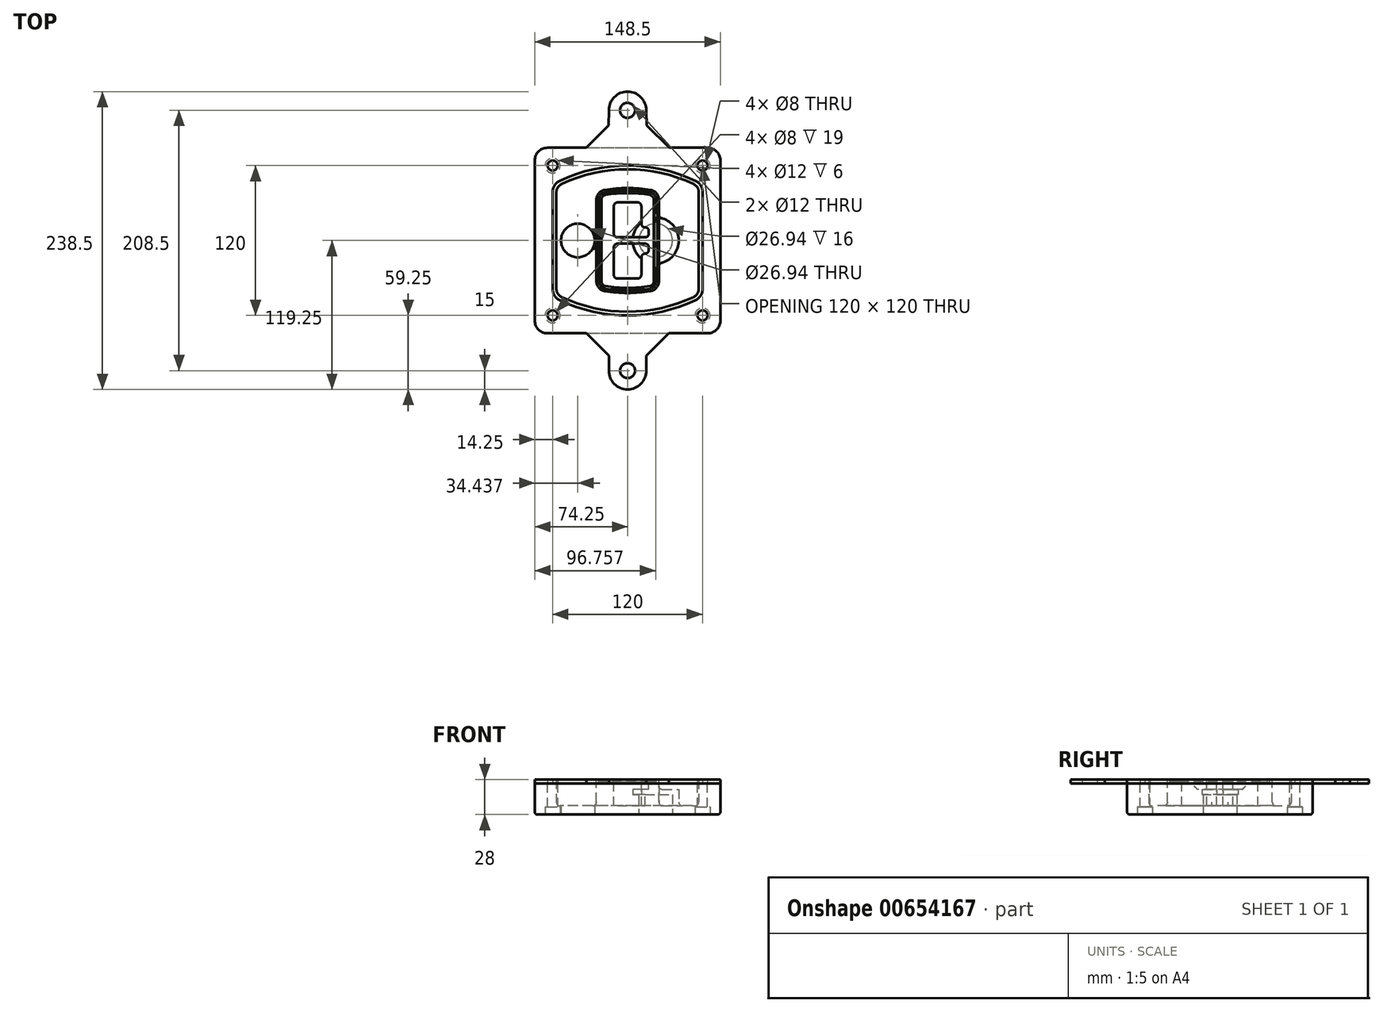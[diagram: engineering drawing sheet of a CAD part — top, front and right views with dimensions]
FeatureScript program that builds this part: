
annotation { "Feature Type Name" : "Feature", "Feature Type Description" : "" }
export const myFeature = defineFeature(function(context is Context, id is Id, definition is map)
    precondition{}
    {
        {
            var Q0;
            Q0=qCreatedBy(makeId("Top.planeOp"),FACE);
            var sketch = newSketch(context, id + "F0", { "sketchPlane" : qUnion([Q0])});
            skPoint(sketch, "E0.rect.middle", {"position": v(0, 0) * mm});
            skLineSegment(sketch, "E1.bottom", {"start": v(-64.25, -74.25) * mm, "end": v(64.25, -74.25) * mm});
            skLineSegment(sketch, "E1.top", {"start": v(-64.25, 74.25) * mm, "end": v(64.25, 74.25) * mm});
            skLineSegment(sketch, "E1.left", {"start": v(-74.25, -64.25) * mm, "end": v(-74.25, 64.25) * mm});
            skLineSegment(sketch, "E1.right", {"start": v(74.25, -64.25) * mm, "end": v(74.25, 64.25) * mm});
            skLineSegment(sketch, "E2", {"start": v(-74.25, 74.25) * mm, "end": v(74.25, -74.25) * mm, "construction": true});
            skLineSegment(sketch, "E3", {"start": v(74.25, 74.25) * mm, "end": v(-74.25, -74.25) * mm, "construction": true});
            skCircle(sketch, "E4", {"center": v(-60, 60) * mm, "radius": 4 * mm});
            skCircle(sketch, "E5", {"center": v(60, 60) * mm, "radius": 4 * mm});
            skCircle(sketch, "E6", {"center": v(60, -60) * mm, "radius": 4 * mm});
            skCircle(sketch, "E7", {"center": v(-60, -60) * mm, "radius": 4 * mm});
            skLineSegment(sketch, "E8", {"start": v(-60, 60) * mm, "end": v(60, 60) * mm, "construction": true});
            skLineSegment(sketch, "E9", {"start": v(60, 60) * mm, "end": v(60, -60) * mm, "construction": true});
            skLineSegment(sketch, "E10", {"start": v(60, -60) * mm, "end": v(-60, -60) * mm, "construction": true});
            skLineSegment(sketch, "E11", {"start": v(-60, -60) * mm, "end": v(-60, 60) * mm, "construction": true});
            skLineSegment(sketch, "E12", {"start": v(-60, 38.83) * mm, "end": v(-60, -38.83) * mm});
            skLineSegment(sketch, "E13", {"start": v(60, 38.83) * mm, "end": v(60, -38.83) * mm});
            skArc(sketch, "E14", {"start": v(54.26, 47.88) * mm, "mid": v(0, 60) * mm, "end": v(-54.26, 47.88) * mm});
            skArc(sketch, "E15", {"start": v(-54.26, -47.88) * mm, "mid": v(0, -60) * mm, "end": v(54.26, -47.88) * mm});
            skLineSegment(sketch, "E16", {"start": v(-60, 0) * mm, "end": v(60, 0) * mm, "construction": true});
            skPoint(sketch, "E17.visualSharp", {"position": v(-60, -45) * mm});
            skArc(sketch, "E17.filletArc", {"start": v(-60, -38.83) * mm, "mid": v(-58.44, -44.2) * mm, "end": v(-54.26, -47.88) * mm});
            skPoint(sketch, "E18.visualSharp", {"position": v(-60, 45) * mm});
            skArc(sketch, "E18.filletArc", {"start": v(-54.26, 47.88) * mm, "mid": v(-58.44, 44.2) * mm, "end": v(-60, 38.83) * mm});
            skPoint(sketch, "E19.visualSharp", {"position": v(60, 45) * mm});
            skArc(sketch, "E19.filletArc", {"start": v(60, 38.83) * mm, "mid": v(58.44, 44.2) * mm, "end": v(54.26, 47.88) * mm});
            skPoint(sketch, "E20.visualSharp", {"position": v(60, -45) * mm});
            skArc(sketch, "E20.filletArc", {"start": v(54.26, -47.88) * mm, "mid": v(58.44, -44.2) * mm, "end": v(60, -38.83) * mm});
            skPoint(sketch, "E21.visualSharp", {"position": v(-74.25, 74.25) * mm});
            skArc(sketch, "E21.filletArc", {"start": v(-64.25, 74.25) * mm, "mid": v(-71.32, 71.32) * mm, "end": v(-74.25, 64.25) * mm});
            skPoint(sketch, "E22.visualSharp", {"position": v(74.25, 74.25) * mm});
            skArc(sketch, "E22.filletArc", {"start": v(74.25, 64.25) * mm, "mid": v(71.32, 71.32) * mm, "end": v(64.25, 74.25) * mm});
            skPoint(sketch, "E23.visualSharp", {"position": v(74.25, -74.25) * mm});
            skArc(sketch, "E23.filletArc", {"start": v(64.25, -74.25) * mm, "mid": v(71.32, -71.32) * mm, "end": v(74.25, -64.25) * mm});
            skPoint(sketch, "E24.visualSharp", {"position": v(-74.25, -74.25) * mm});
            skArc(sketch, "E24.filletArc", {"start": v(-74.25, -64.25) * mm, "mid": v(-71.32, -71.32) * mm, "end": v(-64.25, -74.25) * mm});
            skArc(sketch, "E25.0", {"start": v(57, 38.83) * mm, "mid": v(55.9, 42.58) * mm, "end": v(52.98, 45.17) * mm});
            skLineSegment(sketch, "E25.1", {"start": v(57, 38.83) * mm, "end": v(57, -38.83) * mm});
            skArc(sketch, "E25.2", {"start": v(52.98, -45.17) * mm, "mid": v(55.9, -42.58) * mm, "end": v(57, -38.83) * mm});
            skArc(sketch, "E25.3", {"start": v(-52.98, -45.17) * mm, "mid": v(0, -57) * mm, "end": v(52.98, -45.17) * mm});
            skArc(sketch, "E25.4", {"start": v(-57, -38.83) * mm, "mid": v(-55.9, -42.58) * mm, "end": v(-52.98, -45.17) * mm});
            skArc(sketch, "E25.5", {"start": v(52.98, 45.17) * mm, "mid": v(0, 57) * mm, "end": v(-52.98, 45.17) * mm});
            skLineSegment(sketch, "E25.6", {"start": v(-57, 38.83) * mm, "end": v(-57, -38.83) * mm});
            skArc(sketch, "E25.7", {"start": v(-52.98, 45.17) * mm, "mid": v(-55.9, 42.58) * mm, "end": v(-57, 38.83) * mm});
            skArc(sketch, "E26.0", {"start": v(-55.96, 51.5) * mm, "mid": v(-61.82, 46.33) * mm, "end": v(-64, 38.83) * mm});
            skArc(sketch, "E26.1", {"start": v(55.96, 51.5) * mm, "mid": v(0, 64) * mm, "end": v(-55.96, 51.5) * mm});
            skArc(sketch, "E26.2", {"start": v(64, 38.83) * mm, "mid": v(61.82, 46.33) * mm, "end": v(55.96, 51.5) * mm});
            skLineSegment(sketch, "E26.3", {"start": v(64, 38.83) * mm, "end": v(64, -38.83) * mm});
            skArc(sketch, "E26.4", {"start": v(55.96, -51.5) * mm, "mid": v(61.82, -46.33) * mm, "end": v(64, -38.83) * mm});
            skLineSegment(sketch, "E26.5", {"start": v(-64, 38.83) * mm, "end": v(-64, -38.83) * mm});
            skArc(sketch, "E26.6", {"start": v(-55.96, -51.5) * mm, "mid": v(0, -64) * mm, "end": v(55.96, -51.5) * mm});
            skArc(sketch, "E26.7", {"start": v(-64, -38.83) * mm, "mid": v(-61.82, -46.33) * mm, "end": v(-55.96, -51.5) * mm});
            skLineSegment(sketch, "E27", {"start": v(-33.13, 74.25) * mm, "end": v(-15.13, 92.25) * mm});
            skArc(sketch, "E28", {"start": v(15, 104.25) * mm, "mid": v(0, 119.25) * mm, "end": v(-15, 104.25) * mm});
            skCircle(sketch, "E29", {"center": v(0, 104.25) * mm, "radius": 6 * mm});
            skLineSegment(sketch, "E30", {"start": v(0, 104.25) * mm, "end": v(0, 74.25) * mm, "construction": true});
            skLineSegment(sketch, "E31", {"start": v(15.3, 92.25) * mm, "end": v(33.3, 74.25) * mm});
            skLineSegment(sketch, "E32", {"start": v(0, -74.25) * mm, "end": v(0, -104.25) * mm, "construction": true});
            skCircle(sketch, "E33", {"center": v(0, -104.25) * mm, "radius": 6 * mm});
            skArc(sketch, "E34", {"start": v(15, -104.25) * mm, "mid": v(0, -119.25) * mm, "end": v(-15, -104.25) * mm});
            skLineSegment(sketch, "E35", {"start": v(15, -104.25) * mm, "end": v(15, -92.25) * mm});
            skLineSegment(sketch, "E36", {"start": v(-15, -104.25) * mm, "end": v(-15, -92.25) * mm});
            skLineSegment(sketch, "E37", {"start": v(-15, -92.25) * mm, "end": v(-33, -74.25) * mm});
            skLineSegment(sketch, "E38", {"start": v(15, -92.25) * mm, "end": v(33, -74.25) * mm});
            skLineSegment(sketch, "E39", {"start": v(15.3, 92.25) * mm, "end": v(15, 104.25) * mm});
            skLineSegment(sketch, "E40", {"start": v(-15.13, 92.25) * mm, "end": v(-15, 104.25) * mm});
            skSolve(sketch);
        }
        {
            var Q0;
            Q0=makeQuery(id+"F0.imprint","IMPRINT",FACE,{"disambiguationData":[TD([[makeQuery(id+"F0.imprint","IMPRINT",EDGE,{"derivedFrom":sQuery(id+"F0.wireOp",EDGE,"E1.bottom")}),1.0]])]});
            var Q1;
            Q1=makeQuery(id+"F0.imprint","IMPRINT",FACE,{"disambiguationData":[TD([[makeQuery(id+"F0.imprint","IMPRINT",EDGE,{"derivedFrom":sQuery(id+"F0.wireOp",EDGE,"E12")}),1.0]])]});
            var Q2;
            Q2=makeQuery(id+"F0.imprint","IMPRINT",FACE,{"disambiguationData":[TD([[makeQuery(id+"F0.imprint","IMPRINT",EDGE,{"derivedFrom":sQuery(id+"F0.wireOp",EDGE,"E25.0")}),1.0]])]});
            var Q3;
            Q3=makeQuery(id+"F0.imprint","IMPRINT",FACE,{"disambiguationData":[TD([[makeQuery(id+"F0.imprint","IMPRINT",EDGE,{"derivedFrom":sQuery(id+"F0.wireOp",EDGE,"E12")}),-1.0]])]});
            extrude(context, id + "F1", {"entities" : qUnion([Q0, Q1, Q2, Q3]), "oppositeDirection" : true, "depth" : 25 * mm});
        }
        {
            var Q0;
            Q0=makeQuery(id+"F0.imprint","IMPRINT",FACE,{"disambiguationData":[TD([[makeQuery(id+"F0.imprint","IMPRINT",EDGE,{"derivedFrom":sQuery(id+"F0.wireOp",EDGE,"E12")}),1.0]])]});
            extrude(context, id + "F2", {"entities" : qUnion([Q0]), "operationType" : NewBodyOperationType.ADD, "depth" : 3 * mm});
        }
        {
            var Q0;
            Q0=makeQuery(id+"F0.imprint","IMPRINT",FACE,{"disambiguationData":[TD([[makeQuery(id+"F0.imprint","IMPRINT",EDGE,{"derivedFrom":sQuery(id+"F0.wireOp",EDGE,"E25.0")}),1.0]])]});
            extrude(context, id + "F3", {"entities" : qUnion([Q0]), "operationType" : NewBodyOperationType.REMOVE, "oppositeDirection" : true, "depth" : 18 * mm});
        }
        {
            var Q0;
            Q0=makeQuery(id+"F2.opExtrude","CAP_FACE",FACE,{"disambiguationData":[OSD([sQuery(id+"F0.wireOp",EDGE,"E12"),sQuery(id+"F0.wireOp",EDGE,"E13"),sQuery(id+"F0.wireOp",EDGE,"E14"),sQuery(id+"F0.wireOp",EDGE,"E15"),sQuery(id+"F0.wireOp",EDGE,"E17.filletArc"),sQuery(id+"F0.wireOp",EDGE,"E18.filletArc"),sQuery(id+"F0.wireOp",EDGE,"E19.filletArc"),sQuery(id+"F0.wireOp",EDGE,"E20.filletArc"),sQuery(id+"F0.wireOp",EDGE,"E25.0"),sQuery(id+"F0.wireOp",EDGE,"E25.1"),sQuery(id+"F0.wireOp",EDGE,"E25.2"),sQuery(id+"F0.wireOp",EDGE,"E25.3"),sQuery(id+"F0.wireOp",EDGE,"E25.4"),sQuery(id+"F0.wireOp",EDGE,"E25.5"),sQuery(id+"F0.wireOp",EDGE,"E25.6"),sQuery(id+"F0.wireOp",EDGE,"E25.7")])],"isStart":false});
            var sketch = newSketch(context, id + "F4", { "sketchPlane" : qUnion([Q0])});
            skArc(sketch, "E41.0", {"start": v(-18.34, -40.45) * mm, "mid": v(0, -42) * mm, "end": v(18.34, -40.45) * mm});
            skArc(sketch, "E42.0", {"start": v(18.34, 40.45) * mm, "mid": v(0, 42) * mm, "end": v(-18.34, 40.45) * mm});
            skLineSegment(sketch, "E43", {"start": v(-25, 32.57) * mm, "end": v(-25, -32.57) * mm});
            skLineSegment(sketch, "E44", {"start": v(25, 32.57) * mm, "end": v(25, -32.57) * mm});
            skLineSegment(sketch, "E45", {"start": v(-25, 39.1) * mm, "end": v(25, 39.1) * mm, "construction": true});
            skLineSegment(sketch, "E46", {"start": v(-25, -39.1) * mm, "end": v(25, -39.1) * mm, "construction": true});
            skPoint(sketch, "E47.visualSharp", {"position": v(-25, 39.1) * mm});
            skArc(sketch, "E47.filletArc", {"start": v(-18.34, 40.45) * mm, "mid": v(-23.11, 37.73) * mm, "end": v(-25, 32.57) * mm});
            skPoint(sketch, "E48.visualSharp", {"position": v(25, 39.1) * mm});
            skArc(sketch, "E48.filletArc", {"start": v(25, 32.57) * mm, "mid": v(23.11, 37.73) * mm, "end": v(18.34, 40.45) * mm});
            skPoint(sketch, "E49.visualSharp", {"position": v(25, -39.1) * mm});
            skArc(sketch, "E49.filletArc", {"start": v(18.34, -40.45) * mm, "mid": v(23.11, -37.73) * mm, "end": v(25, -32.57) * mm});
            skPoint(sketch, "E50.visualSharp", {"position": v(-25, -39.1) * mm});
            skArc(sketch, "E50.filletArc", {"start": v(-25, -32.57) * mm, "mid": v(-23.11, -37.73) * mm, "end": v(-18.34, -40.45) * mm});
            skArc(sketch, "E51.0", {"start": v(52.98, 45.17) * mm, "mid": v(0, 57) * mm, "end": v(-52.98, 45.17) * mm});
            skArc(sketch, "E51.1", {"start": v(-52.98, 45.17) * mm, "mid": v(-55.9, 42.58) * mm, "end": v(-57, 38.83) * mm});
            skLineSegment(sketch, "E51.2", {"start": v(-57, 38.83) * mm, "end": v(-57, -38.83) * mm});
            skArc(sketch, "E51.3", {"start": v(-57, -38.83) * mm, "mid": v(-55.9, -42.58) * mm, "end": v(-52.98, -45.17) * mm});
            skArc(sketch, "E51.4", {"start": v(-52.98, -45.17) * mm, "mid": v(0, -57) * mm, "end": v(52.98, -45.17) * mm});
            skArc(sketch, "E51.5", {"start": v(52.98, -45.17) * mm, "mid": v(55.9, -42.58) * mm, "end": v(57, -38.83) * mm});
            skLineSegment(sketch, "E51.6", {"start": v(57, 38.83) * mm, "end": v(57, -38.83) * mm});
            skArc(sketch, "E51.7", {"start": v(57, 38.83) * mm, "mid": v(55.9, 42.58) * mm, "end": v(52.98, 45.17) * mm});
            skLineSegment(sketch, "E52.0", {"start": v(23, 32.57) * mm, "end": v(23, -32.57) * mm});
            skArc(sketch, "E52.1", {"start": v(18, -38.48) * mm, "mid": v(21.58, -36.44) * mm, "end": v(23, -32.57) * mm});
            skArc(sketch, "E52.2", {"start": v(-18, -38.48) * mm, "mid": v(0, -40) * mm, "end": v(18, -38.48) * mm});
            skArc(sketch, "E52.3", {"start": v(-23, -32.57) * mm, "mid": v(-21.58, -36.44) * mm, "end": v(-18, -38.48) * mm});
            skLineSegment(sketch, "E52.4", {"start": v(-23, 32.57) * mm, "end": v(-23, -32.57) * mm});
            skArc(sketch, "E52.5", {"start": v(23, 32.57) * mm, "mid": v(21.58, 36.44) * mm, "end": v(18, 38.48) * mm});
            skArc(sketch, "E52.6", {"start": v(-18, 38.48) * mm, "mid": v(-21.58, 36.44) * mm, "end": v(-23, 32.57) * mm});
            skArc(sketch, "E52.7", {"start": v(18, 38.48) * mm, "mid": v(0, 40) * mm, "end": v(-18, 38.48) * mm});
            skArc(sketch, "E53.0", {"start": v(21, 32.57) * mm, "mid": v(20.06, 35.15) * mm, "end": v(17.67, 36.5) * mm});
            skLineSegment(sketch, "E53.1", {"start": v(21, 32.57) * mm, "end": v(21, -32.57) * mm});
            skArc(sketch, "E53.2", {"start": v(17.67, -36.5) * mm, "mid": v(20.06, -35.15) * mm, "end": v(21, -32.57) * mm});
            skArc(sketch, "E53.3", {"start": v(-17.67, -36.5) * mm, "mid": v(0, -38) * mm, "end": v(17.67, -36.5) * mm});
            skArc(sketch, "E53.4", {"start": v(-21, -32.57) * mm, "mid": v(-20.06, -35.15) * mm, "end": v(-17.67, -36.5) * mm});
            skArc(sketch, "E53.5", {"start": v(17.67, 36.5) * mm, "mid": v(0, 38) * mm, "end": v(-17.67, 36.5) * mm});
            skLineSegment(sketch, "E53.6", {"start": v(-21, 32.57) * mm, "end": v(-21, -32.57) * mm});
            skArc(sketch, "E53.7", {"start": v(-17.67, 36.5) * mm, "mid": v(-20.06, 35.15) * mm, "end": v(-21, 32.57) * mm});
            skLineSegment(sketch, "E54", {"start": v(-25, 0) * mm, "end": v(25, 0) * mm, "construction": true});
            skLineSegment(sketch, "E55", {"start": v(-11, 5.5) * mm, "end": v(-11, 27.5) * mm});
            skLineSegment(sketch, "E56", {"start": v(-8, 30.5) * mm, "end": v(8, 30.5) * mm});
            skLineSegment(sketch, "E57", {"start": v(11, 27.5) * mm, "end": v(11, 13.5) * mm});
            skLineSegment(sketch, "E58", {"start": v(14, 10.5) * mm, "end": v(14, 10.5) * mm});
            skLineSegment(sketch, "E59", {"start": v(17, 7.5) * mm, "end": v(17, 5.5) * mm});
            skLineSegment(sketch, "E60", {"start": v(14, 2.5) * mm, "end": v(-8, 2.5) * mm});
            skPoint(sketch, "E61.visualSharp", {"position": v(-11, 30.5) * mm});
            skArc(sketch, "E61.filletArc", {"start": v(-8, 30.5) * mm, "mid": v(-10.12, 29.62) * mm, "end": v(-11, 27.5) * mm});
            skPoint(sketch, "E62.visualSharp", {"position": v(11, 30.5) * mm});
            skArc(sketch, "E62.filletArc", {"start": v(11, 27.5) * mm, "mid": v(10.12, 29.62) * mm, "end": v(8, 30.5) * mm});
            skPoint(sketch, "E63.visualSharp", {"position": v(11, 10.5) * mm});
            skArc(sketch, "E63.filletArc", {"start": v(11, 13.5) * mm, "mid": v(11.88, 11.38) * mm, "end": v(14, 10.5) * mm});
            skPoint(sketch, "E64.visualSharp", {"position": v(17, 10.5) * mm});
            skArc(sketch, "E64.filletArc", {"start": v(17, 7.5) * mm, "mid": v(16.12, 9.62) * mm, "end": v(14, 10.5) * mm});
            skPoint(sketch, "E65.visualSharp", {"position": v(17, 2.5) * mm});
            skArc(sketch, "E65.filletArc", {"start": v(14, 2.5) * mm, "mid": v(16.12, 3.38) * mm, "end": v(17, 5.5) * mm});
            skPoint(sketch, "E66.visualSharp", {"position": v(-11, 2.5) * mm});
            skArc(sketch, "E66.filletArc", {"start": v(-11, 5.5) * mm, "mid": v(-10.12, 3.38) * mm, "end": v(-8, 2.5) * mm});
            skLineSegment(sketch, "E67.0.MirrorCS", {"start": v(14, -2.5) * mm, "end": v(-8, -2.5) * mm});
            skArc(sketch, "E68.0.MirrorCS", {"start": v(-11, -5.5) * mm, "mid": v(-10.12, -3.38) * mm, "end": v(-8, -2.5) * mm});
            skLineSegment(sketch, "E69.0.MirrorCS", {"start": v(-11, -5.5) * mm, "end": v(-11, -27.5) * mm});
            skArc(sketch, "E70.0.MirrorCS", {"start": v(-8, -30.5) * mm, "mid": v(-10.12, -29.62) * mm, "end": v(-11, -27.5) * mm});
            skLineSegment(sketch, "E71.0.MirrorCS", {"start": v(-8, -30.5) * mm, "end": v(8, -30.5) * mm});
            skArc(sketch, "E72.0.MirrorCS", {"start": v(11, -27.5) * mm, "mid": v(10.12, -29.62) * mm, "end": v(8, -30.5) * mm});
            skLineSegment(sketch, "E73.0.MirrorCS", {"start": v(11, -27.5) * mm, "end": v(11, -13.5) * mm});
            skArc(sketch, "E74.0.MirrorCS", {"start": v(11, -13.5) * mm, "mid": v(11.88, -11.38) * mm, "end": v(14, -10.5) * mm});
            skArc(sketch, "E75.0.MirrorCS", {"start": v(17, -7.5) * mm, "mid": v(16.12, -9.62) * mm, "end": v(14, -10.5) * mm});
            skLineSegment(sketch, "E76.0.MirrorCS", {"start": v(17, -7.5) * mm, "end": v(17, -5.5) * mm});
            skArc(sketch, "E77.0.MirrorCS", {"start": v(14, -2.5) * mm, "mid": v(16.12, -3.38) * mm, "end": v(17, -5.5) * mm});
            skSolve(sketch);
        }
        {
            var Q0;
            Q0=makeQuery(id+"F4.imprint","IMPRINT",FACE,{"disambiguationData":[TD([[makeQuery(id+"F4.imprint","IMPRINT",EDGE,{"derivedFrom":sQuery(id+"F4.wireOp",EDGE,"E41.0")}),1.0]])]});
            var Q1;
            Q1=makeQuery(id+"F4.imprint","IMPRINT",FACE,{"disambiguationData":[TD([[makeQuery(id+"F4.imprint","IMPRINT",EDGE,{"derivedFrom":sQuery(id+"F4.wireOp",EDGE,"E52.0")}),-1.0]])]});
            var Q2;
            Q2=makeQuery(id+"F4.imprint","IMPRINT",FACE,{"disambiguationData":[TD([[makeQuery(id+"F4.imprint","IMPRINT",EDGE,{"derivedFrom":sQuery(id+"F4.wireOp",EDGE,"E53.0")}),1.0]])]});
            extrude(context, id + "F5", {"entities" : qUnion([Q0, Q1, Q2]), "operationType" : NewBodyOperationType.ADD, "endBound" : BoundingType.UP_TO_NEXT, "oppositeDirection" : true, "depth" : 25 * mm});
        }
        {
            var Q0;
            Q0=makeQuery(id+"F4.imprint","IMPRINT",FACE,{"disambiguationData":[TD([[makeQuery(id+"F4.imprint","IMPRINT",EDGE,{"derivedFrom":sQuery(id+"F4.wireOp",EDGE,"E52.0")}),-1.0]])]});
            extrude(context, id + "F6", {"entities" : qUnion([Q0]), "operationType" : NewBodyOperationType.REMOVE, "oppositeDirection" : true, "depth" : 2 * mm});
        }
        {
            var Q0;
            Q0=makeQuery(id+"F1.opExtrude","CAP_FACE",FACE,{"disambiguationData":[OSD([sQuery(id+"F0.wireOp",EDGE,"E1.bottom"),sQuery(id+"F0.wireOp",EDGE,"E1.top"),sQuery(id+"F0.wireOp",EDGE,"E1.left"),sQuery(id+"F0.wireOp",EDGE,"E1.right"),sQuery(id+"F0.wireOp",EDGE,"E4"),sQuery(id+"F0.wireOp",EDGE,"E5"),sQuery(id+"F0.wireOp",EDGE,"E6"),sQuery(id+"F0.wireOp",EDGE,"E7"),sQuery(id+"F0.wireOp",EDGE,"E21.filletArc"),sQuery(id+"F0.wireOp",EDGE,"E22.filletArc"),sQuery(id+"F0.wireOp",EDGE,"E23.filletArc"),sQuery(id+"F0.wireOp",EDGE,"E24.filletArc")])],"isStart":false});
            var sketch = newSketch(context, id + "F7", { "sketchPlane" : qUnion([Q0])});
            skCircle(sketch, "E78", {"center": v(22.5, 0) * mm, "radius": 13.47 * mm});
            skCircle(sketch, "E79", {"center": v(-39.81, 0) * mm, "radius": 13.47 * mm});
            skLineSegment(sketch, "E80", {"start": v(74.25, 0) * mm, "end": v(-74.25, 0) * mm});
            skCircle(sketch, "E81", {"center": v(22.5, 0) * mm, "radius": 18.47 * mm});
            skCircle(sketch, "E82", {"center": v(60, -60) * mm, "radius": 6 * mm});
            skCircle(sketch, "E83", {"center": v(-60, -60) * mm, "radius": 6 * mm});
            skCircle(sketch, "E84", {"center": v(-60, 60) * mm, "radius": 6 * mm});
            skCircle(sketch, "E85", {"center": v(60, 60) * mm, "radius": 6 * mm});
            skSolve(sketch);
        }
        {
            var Q0;
            {var subQ1=sQuery(id+"F7.wireOp",EDGE,"E80");var subQ4=sQuery(id+"F7.wireOp",EDGE,"E78");var subQ6=makeQuery(id+"F7.imprint","INTERSECT",VERTEX,{"disambiguationData":[OD(0.0)],"derivedFrom":[subQ4,subQ1]});Q0=makeQuery(id+"F7.imprint","IMPRINT",FACE,{"disambiguationData":[TD([[makeQuery(id+"F7.imprint","IMPRINT",EDGE,{"disambiguationData":[TD([[subQ6,-1.0]])],"derivedFrom":subQ4}),-1.0]])]});}
            var Q1;
            {var subQ0=sQuery(id+"F7.wireOp",EDGE,"E80");var subQ1=sQuery(id+"F7.wireOp",EDGE,"E78");var subQ3=makeQuery(id+"F7.imprint","INTERSECT",VERTEX,{"disambiguationData":[OD(0.0)],"derivedFrom":[subQ1,subQ0]});Q1=makeQuery(id+"F7.imprint","IMPRINT",FACE,{"disambiguationData":[TD([[makeQuery(id+"F7.imprint","IMPRINT",EDGE,{"disambiguationData":[TD([[subQ3,-1.0]])],"derivedFrom":subQ1}),1.0]])]});}
            var Q2;
            {var subQ0=sQuery(id+"F7.wireOp",EDGE,"E80");var subQ1=sQuery(id+"F7.wireOp",EDGE,"E78");var subQ3=makeQuery(id+"F7.imprint","INTERSECT",VERTEX,{"disambiguationData":[OD(0.0)],"derivedFrom":[subQ1,subQ0]});Q2=makeQuery(id+"F7.imprint","IMPRINT",FACE,{"disambiguationData":[TD([[makeQuery(id+"F7.imprint","IMPRINT",EDGE,{"disambiguationData":[TD([[subQ3,1.0]])],"derivedFrom":subQ1}),1.0]])]});}
            var Q3;
            {var subQ1=sQuery(id+"F7.wireOp",EDGE,"E80");var subQ4=sQuery(id+"F7.wireOp",EDGE,"E78");var subQ6=makeQuery(id+"F7.imprint","INTERSECT",VERTEX,{"disambiguationData":[OD(0.0)],"derivedFrom":[subQ4,subQ1]});Q3=makeQuery(id+"F7.imprint","IMPRINT",FACE,{"disambiguationData":[TD([[makeQuery(id+"F7.imprint","IMPRINT",EDGE,{"disambiguationData":[TD([[subQ6,1.0]])],"derivedFrom":subQ4}),-1.0]])]});}
            extrude(context, id + "F8", {"entities" : qUnion([Q0, Q1, Q2, Q3]), "operationType" : NewBodyOperationType.ADD, "oppositeDirection" : true, "depth" : 20 * mm});
        }
        {
            var Q0;
            {var subQ0=sQuery(id+"F7.wireOp",EDGE,"E80");var subQ1=sQuery(id+"F7.wireOp",EDGE,"E78");var subQ3=makeQuery(id+"F7.imprint","INTERSECT",VERTEX,{"disambiguationData":[OD(0.0)],"derivedFrom":[subQ1,subQ0]});Q0=makeQuery(id+"F7.imprint","IMPRINT",FACE,{"disambiguationData":[TD([[makeQuery(id+"F7.imprint","IMPRINT",EDGE,{"disambiguationData":[TD([[subQ3,-1.0]])],"derivedFrom":subQ1}),1.0]])]});}
            var Q1;
            {var subQ0=sQuery(id+"F7.wireOp",EDGE,"E80");var subQ1=sQuery(id+"F7.wireOp",EDGE,"E78");var subQ3=makeQuery(id+"F7.imprint","INTERSECT",VERTEX,{"disambiguationData":[OD(0.0)],"derivedFrom":[subQ1,subQ0]});Q1=makeQuery(id+"F7.imprint","IMPRINT",FACE,{"disambiguationData":[TD([[makeQuery(id+"F7.imprint","IMPRINT",EDGE,{"disambiguationData":[TD([[subQ3,1.0]])],"derivedFrom":subQ1}),1.0]])]});}
            extrude(context, id + "F9", {"entities" : qUnion([Q0, Q1]), "operationType" : NewBodyOperationType.REMOVE, "oppositeDirection" : true, "depth" : 16 * mm});
        }
        {
            var Q0;
            {var subQ0=sQuery(id+"F7.wireOp",EDGE,"E80");var subQ1=sQuery(id+"F7.wireOp",EDGE,"E79");var subQ3=makeQuery(id+"F7.imprint","INTERSECT",VERTEX,{"disambiguationData":[OD(0.0)],"derivedFrom":[subQ1,subQ0]});Q0=makeQuery(id+"F7.imprint","IMPRINT",FACE,{"disambiguationData":[TD([[makeQuery(id+"F7.imprint","IMPRINT",EDGE,{"disambiguationData":[TD([[subQ3,-1.0]])],"derivedFrom":subQ1}),1.0]])]});}
            var Q1;
            {var subQ0=sQuery(id+"F7.wireOp",EDGE,"E80");var subQ1=sQuery(id+"F7.wireOp",EDGE,"E79");var subQ3=makeQuery(id+"F7.imprint","INTERSECT",VERTEX,{"disambiguationData":[OD(0.0)],"derivedFrom":[subQ1,subQ0]});Q1=makeQuery(id+"F7.imprint","IMPRINT",FACE,{"disambiguationData":[TD([[makeQuery(id+"F7.imprint","IMPRINT",EDGE,{"disambiguationData":[TD([[subQ3,1.0]])],"derivedFrom":subQ1}),1.0]])]});}
            extrude(context, id + "F10", {"entities" : qUnion([Q0, Q1]), "operationType" : NewBodyOperationType.REMOVE, "oppositeDirection" : true, "depth" : 25 * mm});
        }
        {
            var Q0;
            Q0=makeQuery(id+"F7.imprint","IMPRINT",FACE,{"disambiguationData":[TD([[makeQuery(id+"F7.imprint","IMPRINT",EDGE,{"derivedFrom":sQuery(id+"F7.wireOp",EDGE,"E82")}),1.0]])]});
            var Q1;
            Q1=makeQuery(id+"F7.imprint","IMPRINT",FACE,{"disambiguationData":[TD([[makeQuery(id+"F7.imprint","IMPRINT",EDGE,{"derivedFrom":makeQuery(id+"F1.opExtrude","CAP_EDGE",EDGE,{"disambiguationData":[OSD([sQuery(id+"F0.wireOp",EDGE,"E5")])],"isStart":false})}),-1.0]])]});
            var Q2;
            Q2=makeQuery(id+"F7.imprint","IMPRINT",FACE,{"disambiguationData":[TD([[makeQuery(id+"F7.imprint","IMPRINT",EDGE,{"derivedFrom":sQuery(id+"F7.wireOp",EDGE,"E83")}),1.0]])]});
            var Q3;
            Q3=makeQuery(id+"F7.imprint","IMPRINT",FACE,{"disambiguationData":[TD([[makeQuery(id+"F7.imprint","IMPRINT",EDGE,{"derivedFrom":makeQuery(id+"F1.opExtrude","CAP_EDGE",EDGE,{"disambiguationData":[OSD([sQuery(id+"F0.wireOp",EDGE,"E4")])],"isStart":false})}),-1.0]])]});
            var Q4;
            Q4=makeQuery(id+"F7.imprint","IMPRINT",FACE,{"disambiguationData":[TD([[makeQuery(id+"F7.imprint","IMPRINT",EDGE,{"derivedFrom":sQuery(id+"F7.wireOp",EDGE,"E84")}),1.0]])]});
            var Q5;
            Q5=makeQuery(id+"F7.imprint","IMPRINT",FACE,{"disambiguationData":[TD([[makeQuery(id+"F7.imprint","IMPRINT",EDGE,{"derivedFrom":makeQuery(id+"F1.opExtrude","CAP_EDGE",EDGE,{"disambiguationData":[OSD([sQuery(id+"F0.wireOp",EDGE,"E7")])],"isStart":false})}),-1.0]])]});
            var Q6;
            Q6=makeQuery(id+"F7.imprint","IMPRINT",FACE,{"disambiguationData":[TD([[makeQuery(id+"F7.imprint","IMPRINT",EDGE,{"derivedFrom":sQuery(id+"F7.wireOp",EDGE,"E85")}),1.0]])]});
            var Q7;
            Q7=makeQuery(id+"F7.imprint","IMPRINT",FACE,{"disambiguationData":[TD([[makeQuery(id+"F7.imprint","IMPRINT",EDGE,{"derivedFrom":makeQuery(id+"F1.opExtrude","CAP_EDGE",EDGE,{"disambiguationData":[OSD([sQuery(id+"F0.wireOp",EDGE,"E6")])],"isStart":false})}),-1.0]])]});
            extrude(context, id + "F11", {"entities" : qUnion([Q0, Q1, Q2, Q3, Q4, Q5, Q6, Q7]), "operationType" : NewBodyOperationType.REMOVE, "oppositeDirection" : true, "depth" : 6 * mm});
        }
        {
            var Q0;
            Q0=makeQuery(id+"F9.boolean.opBoolean","COPY",FACE,{"derivedFrom":makeQuery(id+"F9.opExtrude","CAP_FACE",FACE,{"disambiguationData":[OSD([sQuery(id+"F7.wireOp",EDGE,"E78")])],"isStart":false})});
            var sketch = newSketch(context, id + "F12", { "sketchPlane" : qUnion([Q0])});
            skArc(sketch, "E86.0", {"start": v(11, 14.45) * mm, "mid": v(6.45, 9.13) * mm, "end": v(4.2, 2.5) * mm});
            skArc(sketch, "E86.1", {"start": v(4.2, -2.5) * mm, "mid": v(6.45, -9.13) * mm, "end": v(11, -14.45) * mm});
            skLineSegment(sketch, "E87", {"start": v(4.2, -2.5) * mm, "end": v(14, -2.5) * mm});
            skLineSegment(sketch, "E88.0", {"start": v(14, 2.5) * mm, "end": v(4.2, 2.5) * mm});
            skArc(sketch, "E88.1", {"start": v(14, 2.5) * mm, "mid": v(16.12, 3.38) * mm, "end": v(17, 5.5) * mm});
            skLineSegment(sketch, "E88.2", {"start": v(17, 7.5) * mm, "end": v(17, 5.5) * mm});
            skArc(sketch, "E88.3", {"start": v(17, 7.5) * mm, "mid": v(16.12, 9.62) * mm, "end": v(14, 10.5) * mm});
            skArc(sketch, "E88.4", {"start": v(11, 13.5) * mm, "mid": v(11.88, 11.38) * mm, "end": v(14, 10.5) * mm});
            skLineSegment(sketch, "E88.5", {"start": v(11, 14.45) * mm, "end": v(11, 13.5) * mm});
            skLineSegment(sketch, "E88.7", {"start": v(14, -2.5) * mm, "end": v(4.2, -2.5) * mm});
            skArc(sketch, "E88.8", {"start": v(14, -2.5) * mm, "mid": v(16.12, -3.38) * mm, "end": v(17, -5.5) * mm});
            skLineSegment(sketch, "E88.9", {"start": v(17, -7.5) * mm, "end": v(17, -5.5) * mm});
            skArc(sketch, "E88.10", {"start": v(17, -7.5) * mm, "mid": v(16.12, -9.62) * mm, "end": v(14, -10.5) * mm});
            skArc(sketch, "E88.11", {"start": v(11, -13.5) * mm, "mid": v(11.88, -11.38) * mm, "end": v(14, -10.5) * mm});
            skLineSegment(sketch, "E88.12", {"start": v(11, -14.45) * mm, "end": v(11, -13.5) * mm});
            skPoint(sketch, "E89.orphan", {"position": v(11, -27.5) * mm});
            skPoint(sketch, "E90.orphan", {"position": v(-8, -2.5) * mm});
            skPoint(sketch, "E91.orphan", {"position": v(-8, 2.5) * mm});
            skPoint(sketch, "E92.orphan", {"position": v(11, 27.5) * mm});
            skSolve(sketch);
        }
        {
            var Q0;
            {var subQ7=sQuery(id+"F12.wireOp",EDGE,"E86.0");var subQ14=sQuery(id+"F12.wireOp",EDGE,"E86.1");var subQ16=sQuery(id+"F12.wireOp",EDGE,"E88.1");var subQ18=sQuery(id+"F12.wireOp",EDGE,"E88.8");Q0=qUnion([makeQuery(id+"F12.imprint","IMPRINT",FACE,{"disambiguationData":[TD([[makeQuery(id+"F12.imprint","IMPRINT",EDGE,{"derivedFrom":subQ7}),1.0]])]}),makeQuery(id+"F12.imprint","IMPRINT",FACE,{"disambiguationData":[TD([[makeQuery(id+"F12.imprint","IMPRINT",EDGE,{"derivedFrom":subQ14}),1.0]])]}),makeQuery(id+"F12.imprint","IMPRINT",FACE,{"disambiguationData":[TD([[makeQuery(id+"F12.imprint","IMPRINT",EDGE,{"derivedFrom":subQ16}),1.0]])]}),makeQuery(id+"F12.imprint","IMPRINT",FACE,{"disambiguationData":[TD([[makeQuery(id+"F12.imprint","IMPRINT",EDGE,{"derivedFrom":subQ18}),-1.0]])]})]);}
            var Q1;
            Q1=makeQuery(id+"F5.boolean.opBoolean","SPLIT",FACE,{"disambiguationData":[TD([makeQuery(id+"F5.opExtrude","SWEPT_FACE",FACE,{"disambiguationData":[OSD([sQuery(id+"F4.wireOp",EDGE,"E55")])]})])],"derivedFrom":makeQuery(id+"F3.boolean.opBoolean","COPY",FACE,{"derivedFrom":makeQuery(id+"F3.opExtrude","CAP_FACE",FACE,{"disambiguationData":[OSD([sQuery(id+"F0.wireOp",EDGE,"E25.0"),sQuery(id+"F0.wireOp",EDGE,"E25.1"),sQuery(id+"F0.wireOp",EDGE,"E25.2"),sQuery(id+"F0.wireOp",EDGE,"E25.3"),sQuery(id+"F0.wireOp",EDGE,"E25.4"),sQuery(id+"F0.wireOp",EDGE,"E25.5"),sQuery(id+"F0.wireOp",EDGE,"E25.6"),sQuery(id+"F0.wireOp",EDGE,"E25.7")])],"isStart":false})})});
            extrude(context, id + "F13", {"entities" : qUnion([Q0]), "operationType" : NewBodyOperationType.REMOVE, "endBound" : BoundingType.UP_TO_SURFACE, "endBoundEntityFace" : qUnion([Q1]), "depth" : 25 * mm});
        }
        {
            var Q0;
            Q0=makeQuery(id+"F3.boolean.opBoolean","COPY",EDGE,{"derivedFrom":makeQuery(id+"F3.opExtrude","CAP_EDGE",EDGE,{"disambiguationData":[OSD([sQuery(id+"F0.wireOp",EDGE,"E25.6")])],"isStart":false})});
            var Q1;
            Q1=makeQuery(id+"F8.boolean.opBoolean","INTERSECT",EDGE,{"derivedFrom":[makeQuery(id+"F5.opExtrude","SWEPT_FACE",FACE,{"disambiguationData":[OSD([sQuery(id+"F4.wireOp",EDGE,"E44")])]}),makeQuery(id+"F8.opExtrude","CAP_FACE",FACE,{"disambiguationData":[OSD([sQuery(id+"F7.wireOp",EDGE,"E81")])],"isStart":false})]});
            var Q2;
            Q2=makeQuery(id+"F8.boolean.opBoolean","INTERSECT",EDGE,{"disambiguationData":[OD(1.0)],"derivedFrom":[makeQuery(id+"F5.opExtrude","SWEPT_FACE",FACE,{"disambiguationData":[OSD([sQuery(id+"F4.wireOp",EDGE,"E44")])]}),makeQuery(id+"F8.opExtrude","SWEPT_FACE",FACE,{"disambiguationData":[OSD([sQuery(id+"F7.wireOp",EDGE,"E81")])]})]});
            var Q3;
            {var subQ0=sQuery(id+"F4.wireOp",EDGE,"E44");Q3=makeQuery(id+"F8.boolean.opBoolean","SPLIT",EDGE,{"disambiguationData":[TD([makeQuery(id+"F5.opExtrude","SWEPT_FACE",FACE,{"disambiguationData":[OSD([sQuery(id+"F4.wireOp",EDGE,"E49.filletArc")])]})])],"derivedFrom":makeQuery(id+"F5.opExtrude","CAP_EDGE",EDGE,{"disambiguationData":[OSD([subQ0])],"isStart":false})});}
            var Q4;
            {var subQ0=sQuery(id+"F0.wireOp",EDGE,"E25.7");var subQ1=sQuery(id+"F0.wireOp",EDGE,"E25.1");var subQ2=sQuery(id+"F0.wireOp",EDGE,"E25.6");var subQ3=sQuery(id+"F0.wireOp",EDGE,"E25.5");var subQ4=sQuery(id+"F0.wireOp",EDGE,"E25.4");var subQ5=sQuery(id+"F0.wireOp",EDGE,"E25.0");var subQ6=sQuery(id+"F0.wireOp",EDGE,"E25.2");var subQ7=sQuery(id+"F0.wireOp",EDGE,"E25.3");Q4=makeQuery(id+"F8.boolean.opBoolean","INTERSECT",EDGE,{"derivedFrom":[makeQuery(id+"F5.boolean.opBoolean","SPLIT",FACE,{"disambiguationData":[TD([makeQuery(id+"F2.opExtrude","SWEPT_FACE",FACE,{"disambiguationData":[OSD([subQ5])]})])],"derivedFrom":makeQuery(id+"F3.boolean.opBoolean","COPY",FACE,{"derivedFrom":makeQuery(id+"F3.opExtrude","CAP_FACE",FACE,{"disambiguationData":[OSD([subQ5,subQ1,subQ6,subQ7,subQ4,subQ3,subQ2,subQ0])],"isStart":false})})}),makeQuery(id+"F8.opExtrude","SWEPT_FACE",FACE,{"disambiguationData":[OSD([sQuery(id+"F7.wireOp",EDGE,"E81")])]})]});}
            var Q5;
            Q5=makeQuery(id+"F8.boolean.opBoolean","INTERSECT",EDGE,{"disambiguationData":[OD(0.0)],"derivedFrom":[makeQuery(id+"F5.opExtrude","SWEPT_FACE",FACE,{"disambiguationData":[OSD([sQuery(id+"F4.wireOp",EDGE,"E44")])]}),makeQuery(id+"F8.opExtrude","SWEPT_FACE",FACE,{"disambiguationData":[OSD([sQuery(id+"F7.wireOp",EDGE,"E81")])]})]});
            fillet(context, id + "F14", {"entities" : qUnion([Q0, Q1, Q2, Q3, Q4, Q5]), "radius" : 3 * mm, "tangentPropagation" : true, "allowEdgeOverflow" : false});
        }
        {
            var Q0;
            Q0=makeQuery(id+"F1.opExtrude","CAP_EDGE",EDGE,{"disambiguationData":[OSD([sQuery(id+"F0.wireOp",EDGE,"E1.bottom")])],"isStart":false});
            fillet(context, id + "F15", {"entities" : qUnion([Q0]), "radius" : 2 * mm, "tangentPropagation" : true, "allowEdgeOverflow" : false});
        }
        {
            var Q0;
            Q0 = qSketchRegion(id + "F0", true);
            var Q1;
            Q1=makeQuery(id+"F0.imprint","IMPRINT",FACE,{"disambiguationData":[TD([[makeQuery(id+"F0.imprint","IMPRINT",EDGE,{"derivedFrom":sQuery(id+"F0.wireOp",EDGE,"E12")}),-1.0]])]});
            var Q2;
            Q2=makeQuery(id+"F2.opExtrude","CAP_FACE",FACE,{"disambiguationData":[OSD([sQuery(id+"F0.wireOp",EDGE,"E12"),sQuery(id+"F0.wireOp",EDGE,"E13"),sQuery(id+"F0.wireOp",EDGE,"E14"),sQuery(id+"F0.wireOp",EDGE,"E15"),sQuery(id+"F0.wireOp",EDGE,"E17.filletArc"),sQuery(id+"F0.wireOp",EDGE,"E18.filletArc"),sQuery(id+"F0.wireOp",EDGE,"E19.filletArc"),sQuery(id+"F0.wireOp",EDGE,"E20.filletArc"),sQuery(id+"F0.wireOp",EDGE,"E25.0"),sQuery(id+"F0.wireOp",EDGE,"E25.1"),sQuery(id+"F0.wireOp",EDGE,"E25.2"),sQuery(id+"F0.wireOp",EDGE,"E25.3"),sQuery(id+"F0.wireOp",EDGE,"E25.4"),sQuery(id+"F0.wireOp",EDGE,"E25.5"),sQuery(id+"F0.wireOp",EDGE,"E25.6"),sQuery(id+"F0.wireOp",EDGE,"E25.7")])],"isStart":false});
            extrude(context, id + "F16", {"entities" : qUnion([Q0, Q1]), "endBound" : BoundingType.UP_TO_SURFACE, "depth" : 25 * mm, "endBoundEntityFace" : qUnion([Q2]), "offsetDistance" : 25 * mm});
        }
    });
